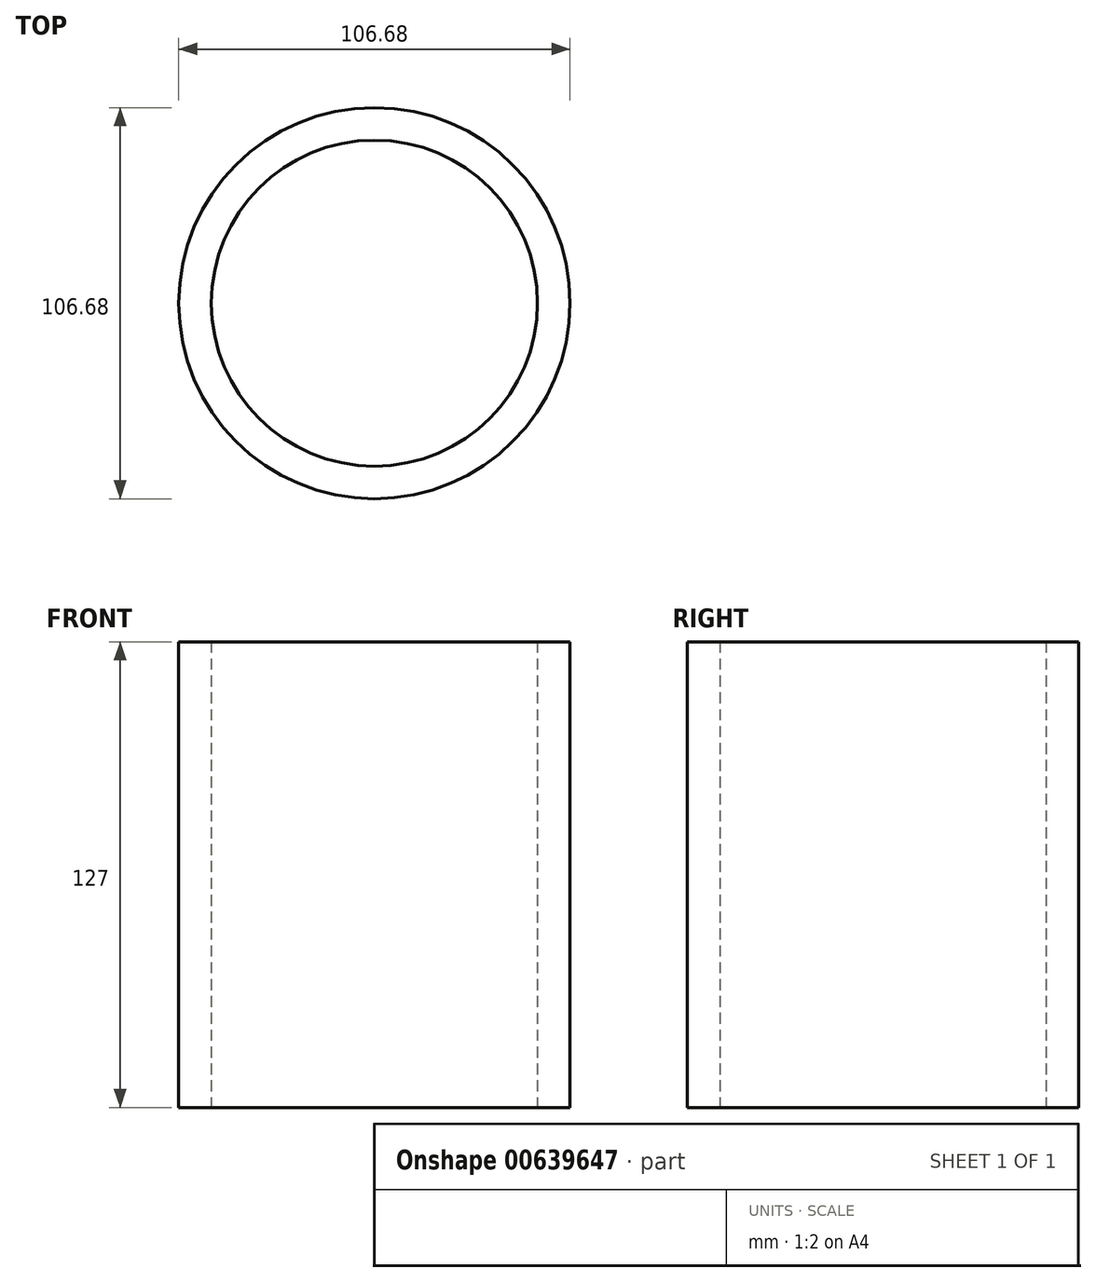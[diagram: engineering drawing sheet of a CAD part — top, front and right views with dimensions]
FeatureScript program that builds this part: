
annotation { "Feature Type Name" : "Feature", "Feature Type Description" : "" }
export const myFeature = defineFeature(function(context is Context, id is Id, definition is map)
    precondition{}
    {
        {
            var Q0;
            Q0=qCreatedBy(makeId("Top.planeOp"),FACE);
            var sketch = newSketch(context, id + "F0", { "sketchPlane" : qUnion([Q0])});
            skCircle(sketch, "E0", {"center": v(0, 0) * mm, "radius": 44.45 * mm});
            skCircle(sketch, "E1", {"center": v(0, 0) * mm, "radius": 53.34 * mm});
            skSolve(sketch);
        }
        {
            var Q0;
            Q0 = qSketchRegion(id + "F0", true);
            var Q1;
            Q1=makeQuery(id+"F0.imprint","IMPRINT",FACE,{"disambiguationData":[TD([[makeQuery(id+"F0.imprint","IMPRINT",EDGE,{"derivedFrom":sQuery(id+"F0.wireOp",EDGE,"E0")}),-1.0]])]});
            extrude(context, id + "F1", {"entities" : qUnion([Q0, Q1]), "depth" : 127 * mm, "offsetDistance" : 25.4 * mm});
        }
    });
